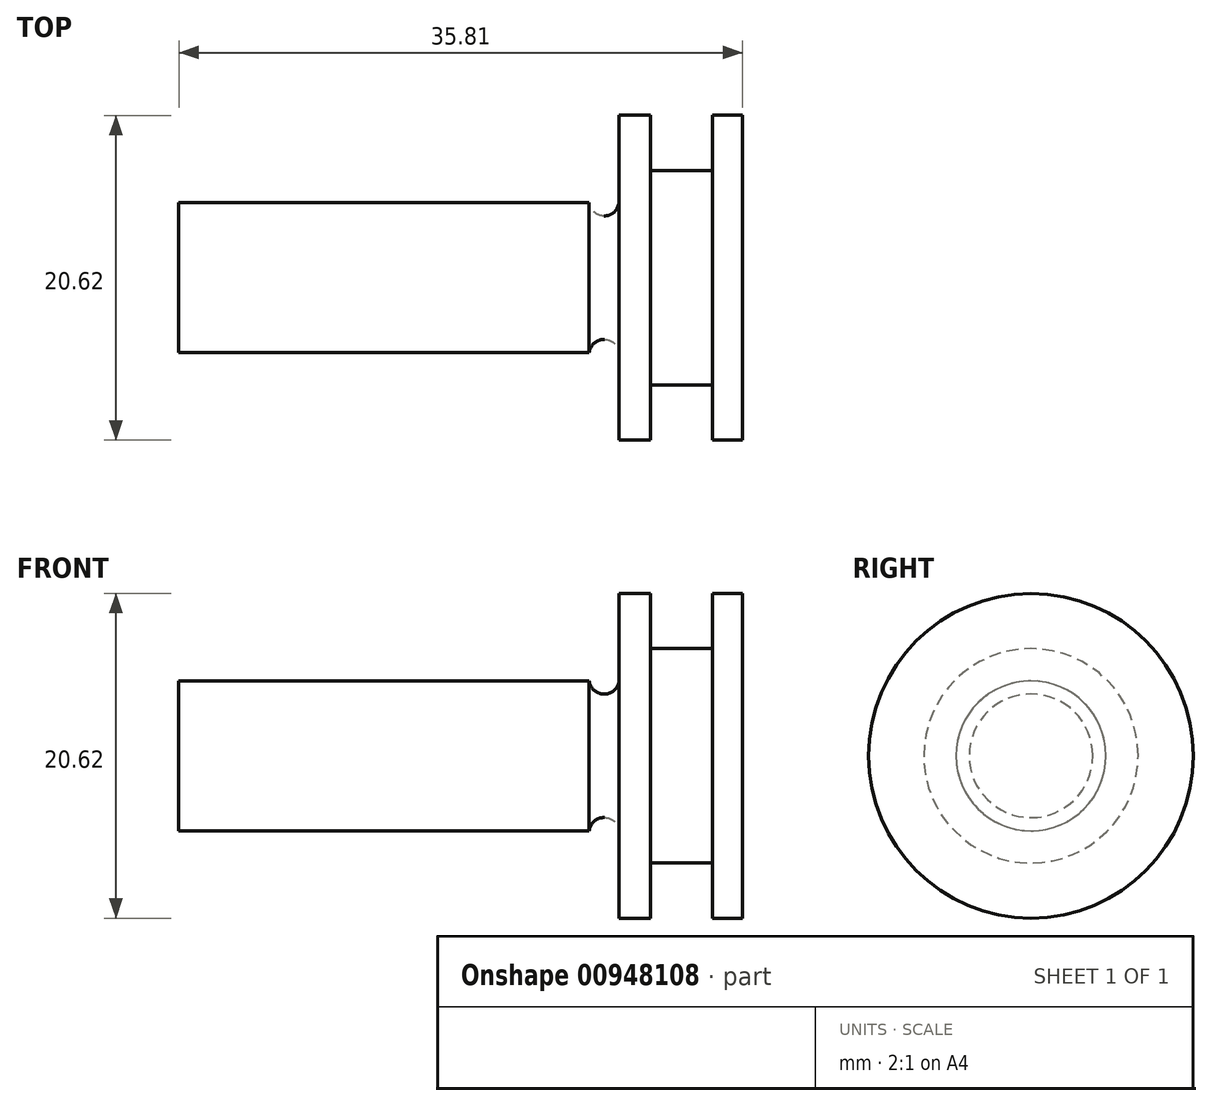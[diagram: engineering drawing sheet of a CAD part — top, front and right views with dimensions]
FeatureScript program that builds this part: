
annotation { "Feature Type Name" : "Feature", "Feature Type Description" : "" }
export const myFeature = defineFeature(function(context is Context, id is Id, definition is map)
    precondition{}
    {
        {
            var Q0;
            Q0=qCreatedBy(makeId("Front.planeOp"),FACE);
            var sketch = newSketch(context, id + "F0", { "sketchPlane" : qUnion([Q0])});
            skLineSegment(sketch, "E0", {"start": v(0, 0) * mm, "end": v(-55.61, 0) * mm, "construction": true});
            skLineSegment(sketch, "E1", {"start": v(0, 0) * mm, "end": v(0, 10.31) * mm});
            skLineSegment(sketch, "E2", {"start": v(0, 10.31) * mm, "end": v(-1.9, 10.31) * mm});
            skLineSegment(sketch, "E3", {"start": v(-1.9, 10.31) * mm, "end": v(-1.9, 6.8) * mm});
            skLineSegment(sketch, "E4", {"start": v(-1.9, 6.8) * mm, "end": v(-5.87, 6.8) * mm});
            skLineSegment(sketch, "E5", {"start": v(-5.87, 6.8) * mm, "end": v(-5.87, 10.31) * mm});
            skLineSegment(sketch, "E6", {"start": v(-5.87, 10.31) * mm, "end": v(-7.85, 10.31) * mm});
            skLineSegment(sketch, "E7", {"start": v(-7.85, 10.31) * mm, "end": v(-7.85, 3.92) * mm});
            skLineSegment(sketch, "E8", {"start": v(-7.85, 3.92) * mm, "end": v(-9.75, 3.92) * mm});
            skLineSegment(sketch, "E9", {"start": v(-9.75, 3.92) * mm, "end": v(-9.75, 4.76) * mm});
            skLineSegment(sketch, "E10", {"start": v(-9.75, 4.76) * mm, "end": v(-35.81, 4.76) * mm});
            skLineSegment(sketch, "E11", {"start": v(-35.81, 4.76) * mm, "end": v(-35.81, 0) * mm});
            skLineSegment(sketch, "E12", {"start": v(-35.81, 0) * mm, "end": v(0, 0) * mm});
            skSolve(sketch);
        }
        {
            var Q0;
            Q0 = qSketchRegion(id + "F0", true);
            var Q1;
            Q1=sQuery(id+"F0.wireOp",EDGE,"E0");
            revolve(context, id + "F1", {"surfaceOperationType" : NewSurfaceOperationType.NEW, "entities" : qUnion([Q0]), "axis" : qUnion([Q1]), "revolveType" : RevolveType.FULL});
        }
        {
            var Q0;
            Q0=makeQuery(id+"F1.opRevolve","SWEPT_EDGE",EDGE,{"disambiguationData":[OSD([sQuery(id+"F0.wireOp",EDGE,"E7"),sQuery(id+"F0.wireOp",EDGE,"E8")])]});
            var Q1;
            Q1=makeQuery(id+"F1.opRevolve","SWEPT_EDGE",EDGE,{"disambiguationData":[OSD([sQuery(id+"F0.wireOp",EDGE,"E8"),sQuery(id+"F0.wireOp",EDGE,"E9")])]});
            fillet(context, id + "F2", {"entities" : qUnion([Q0, Q1]), "radius" : 0.94 * mm, "tangentPropagation" : true, "allowEdgeOverflow" : false});
        }
    });
